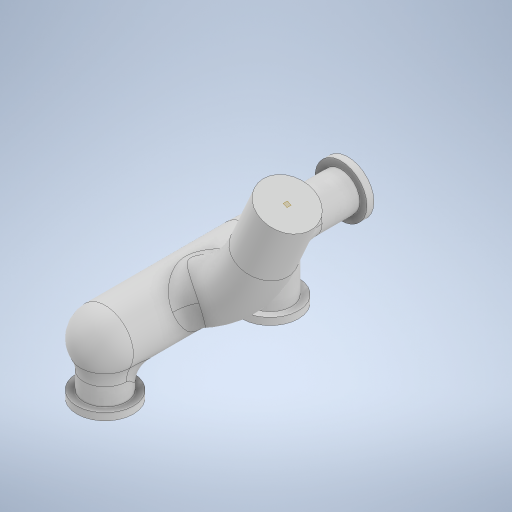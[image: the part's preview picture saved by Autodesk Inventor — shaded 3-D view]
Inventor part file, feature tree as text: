
AUTODESK INVENTOR PART (.ipt)
format: ipt  version: 2023 (Build 270158000, 158)  size: 619,008 bytes
history: native  units: in
note: dims shown in document units (in); Inventor stores cm internally (conversion verified against a paired STEP export)
features: sketch x7, extrude x5, fillet x3, other x2, plane x2, revolve x1, loft x1, sweep x1, mirror x1, projected_geometry x1
ambient origin geometry x8: Origin, YZ Plane, XZ Plane, XY Plane, X Axis, Y Axis, Z Axis, Center Point
bodies: Solid1 (feature_tree)
feature tree (24):
  other  "intake_manifold_f"
  revolve  "Revolution1"  [1 undecoded]
  plane  "Work Plane1"
  loft  "Loft1"
  extrude  "Extrusion1"  Depth=2.0in
  fillet  "Fillet1"  Radius=0.3937in
  extrude  "Extrusion2"  Depth=9.0in
  extrude  "Extrusion3"  Depth=11.0in TaperAngle=0.0deg
  extrude  "Extrusion4"  Depth=12.0in
  sketch  "Sketch9"  dims[d20=12.0in d21=12.0in]
  plane  "Work Plane2"
  sweep  "Sweep2"
  fillet  "Fillet5"  Radius=1.0in
  extrude  "Extrusion6"  Depth=8.0in
  fillet  "Fillet6"  Radius=8.0in
  mirror  "Mirror3"
  sketch  "Sketch3"  dims[d3=30.0in d4=6.0in]
  other  "Edges1"
  sketch  "Sketch4"  dims[d5=90.0deg d6=12.0in]
  sketch  "Sketch5"  dims[d7=8.0in d8=2.0in d9=0.3937in d10=90.0deg]
  projected_geometry  "Projected Loop1"
  sketch  "Sketch6"  dims[d13=0.3937in d14=90.0deg d15=9.0in]
  sketch  "Sketch7"  dims[d16=9.0in d17=11.0in d18=0.0in]
  sketch  "Sketch10"  dims[d22=1.5in d23=0.0in d24=6.0in d25=6.0in d26=6.0in d27=0.0in d28=2.0in d29=0.1969in d30=6.0in d31=0.3937in d33=1.0in d34=0.0in d35=8.0in d36=8.0in d37=0.0in d52=11.0in d56=0.0in d57=0.0in d58=3.0in d59=0.0in d60=5.0in d61=11.0in d62=1.5in d63=0.0in d64=3.0in d65=3.0in d66=3.0in d67=0.0in d68=2.0in d69=0.1291in d70=3.0in d71=0.2583in d72=2.0in d73=0.326in d74=2.5in]
note: 1 required parameter value undecoded (feature->parameter linkage not recoverable at this tier; creation-order binding heuristic only, values carry confidence <= 0.55)
